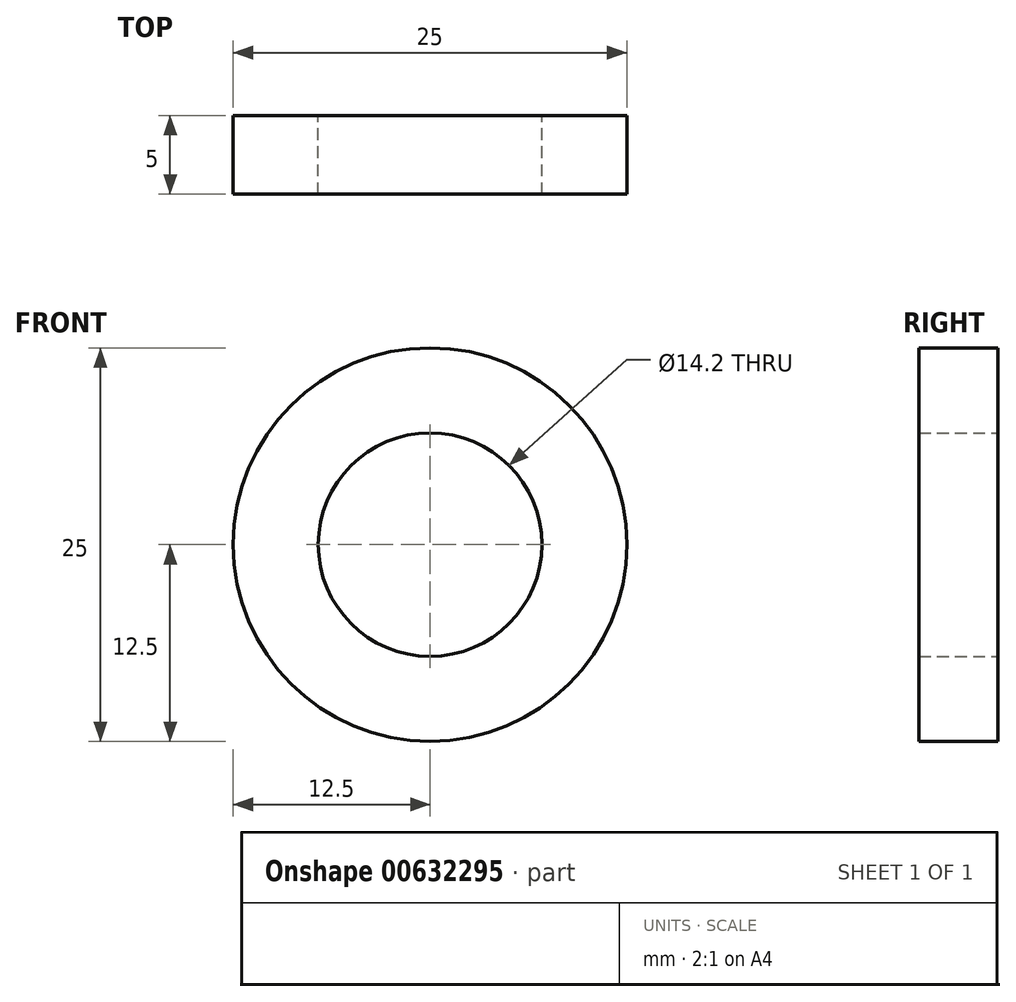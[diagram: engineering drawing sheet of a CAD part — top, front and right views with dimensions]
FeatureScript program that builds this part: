
annotation { "Feature Type Name" : "Feature", "Feature Type Description" : "" }
export const myFeature = defineFeature(function(context is Context, id is Id, definition is map)
    precondition{}
    {
        {
            var Q0;
            Q0=qCreatedBy(makeId("Front.planeOp"),FACE);
            var sketch = newSketch(context, id + "F0", { "sketchPlane" : qUnion([Q0])});
            skCircle(sketch, "E0", {"center": v(0, 0) * mm, "radius": 12.5 * mm});
            skCircle(sketch, "E1", {"center": v(0, 0) * mm, "radius": 7.1 * mm});
            skSolve(sketch);
        }
        {
            var Q0;
            Q0=makeQuery(id+"F0.imprint","IMPRINT",FACE,{"disambiguationData":[TD([[makeQuery(id+"F0.imprint","IMPRINT",EDGE,{"derivedFrom":sQuery(id+"F0.wireOp",EDGE,"E0")}),1.0]])]});
            extrude(context, id + "F1", {"entities" : qUnion([Q0]), "depth" : 5 * mm, "offsetDistance" : 25 * mm});
        }
    });
